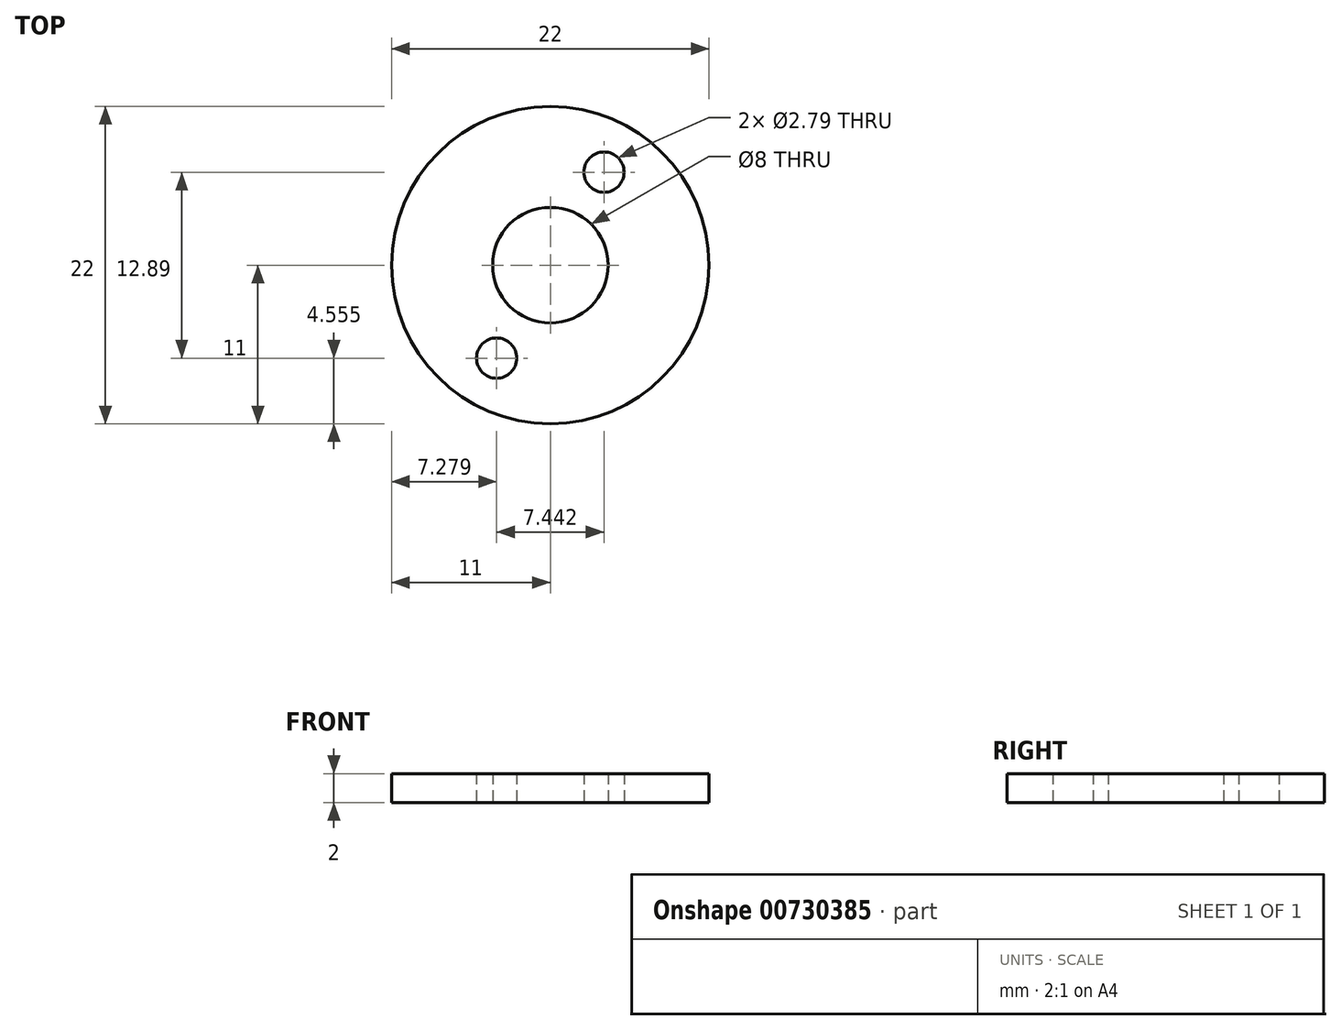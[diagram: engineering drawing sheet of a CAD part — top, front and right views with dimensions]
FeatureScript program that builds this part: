
annotation { "Feature Type Name" : "Feature", "Feature Type Description" : "" }
export const myFeature = defineFeature(function(context is Context, id is Id, definition is map)
    precondition{}
    {
        {
            var Q0;
            Q0=qCreatedBy(makeId("Top.planeOp"),FACE);
            var sketch = newSketch(context, id + "F0", { "sketchPlane" : qUnion([Q0])});
            skCircle(sketch, "E0", {"center": v(0, 0) * mm, "radius": 11 * mm});
            skCircle(sketch, "E1", {"center": v(0, 0) * mm, "radius": 7.44 * mm, "construction": true});
            skCircle(sketch, "E2", {"center": v(0, 0) * mm, "radius": 4 * mm});
            skCircle(sketch, "E3", {"center": v(3.72, 6.45) * mm, "radius": 1.4 * mm});
            skCircle(sketch, "E4.1.0", {"center": v(-3.72, -6.45) * mm, "radius": 1.4 * mm});
            skLineSegment(sketch, "E5", {"start": v(0, 0) * mm, "end": v(3.72, 6.45) * mm, "construction": true});
            skSolve(sketch);
        }
        {
            var Q0;
            Q0=makeQuery(id+"F0.imprint","IMPRINT",FACE,{"disambiguationData":[TD([[makeQuery(id+"F0.imprint","IMPRINT",EDGE,{"derivedFrom":sQuery(id+"F0.wireOp",EDGE,"E0")}),1.0]])]});
            extrude(context, id + "F1", {"entities" : qUnion([Q0]), "depth" : 2 * mm, "offsetDistance" : 25 * mm});
        }
    });
